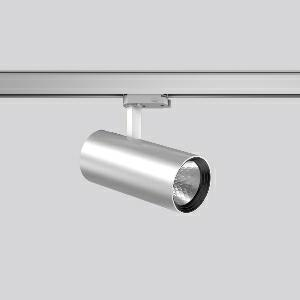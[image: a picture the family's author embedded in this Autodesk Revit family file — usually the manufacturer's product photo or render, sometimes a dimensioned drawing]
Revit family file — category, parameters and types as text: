
# Revit family: deecos_s_mini_742203_004_3_74e2
name_source: partatom
category: Lighting Fixtures
units: mm (PartAtom-declared; Revit-internal decimal feet)

## family parameters
Cut with Voids When Loaded = No
Host = Face
Light Source = No
Part Type = Normal
Room Calculation Point = No
Round Connector Dimension = Use Diameter
Shared = No

## types (1)
- DEECOS S mini (1 x LED Modul 935, 3700 lm, 3500)
    Apparent Load = 29 VA
    Approval mark = CE
    CIE Flux Codes = 100 100 100 100 100
    Color Rendering = 92
    Color Temperature = 3500
    Default Elevation = 1800 mm
    Description = Series: DEECOS S mini
LED surface-mounted projector in modern design with no visible cooling ribs. Housing: die-cast aluminium, powder-coated. Rotation range: 356°. Swivel range: 90°. Black plastic ring and recessed LED to prevent glare from the side. Optical assembly with reflector made of MIRO-Silver with 98% total light reflection for outstanding efficiency - can be changed without tools. Best colour rendering index Ra>90. With multi adaptor for 3-circuit tracks 230 V. Suitable for Track on ceiling, Wall track. High quality converter without flickering and stroboscopic effect. The following accessories can be mounted without use of tools: interchangeable lenses, decorative glasses, honeycomb louvre, clear and frosted diffusers, white interchangeable plastic ring. 
Colour: silver
Diameter: 87 mm
Height: 214 mm
Lamp: LED
Socket: without socket
Colour temperature: 3500K
Colour rendering index (CRI): 92
System power: 29 W
Rated luminous flux: 3700 lm
Luminous efficiency: 128 lm/W
Control gear: Regulated power supply
Protection class: I
Type of protection: IP 20
    Height = 214 mm
    Lamp = 1 x LED Modul 935
    Lamp Light Flux = 3700 lm
    Lamp count = 1
    Length = 87 mm
    Lifetime = 50000 h
    Luminous efficacy = 128 lm/W
    Manufacturer = RZB
    ModVariant = No
    Model = 742203.004.3
    Mounting Place = Ceiling
    Mounting Type = Rail mounted
    Number of Poles = 1
    OnlyDefault = Yes
    Power Factor = 1
    Product Name = DEECOS S mini
    Product group = Track mounted projectors
    ProductGroupID = 301
    Protection Class = Protection class I
    Protection Degree = IP 20
    RLX_Detail_Level = 1
    RLX_Emergency_Light_Flux = 0 lm
    RLX_Emergency_Type = 0
    RLX_Emergency_Type_DB = No
    RlxData = <blob elided: 37489 chars, md5=02653788>
    Socket = socket
    Standby Power = 0 W
    System Light Flux = 3700 lm
    System Power = 29 W
    Type Comments = Product without accessories
    Type Image = 741926.004.jpg
    URL = http://relux.com
    VarID = ---
    Voltage = 230 V
    Voltage Range = 220-240 V
    Weight = 0.00 kg
    Width = 0 mm  [stored 0 ft]

note: [stored X ft] marks values corroborated as IEEE doubles in the binary element streams (Revit-internal decimal feet)

## geometry (parser evidence)
native form markers: Blend x4, Sweep x13
no freeform markers — native parametric forms only
